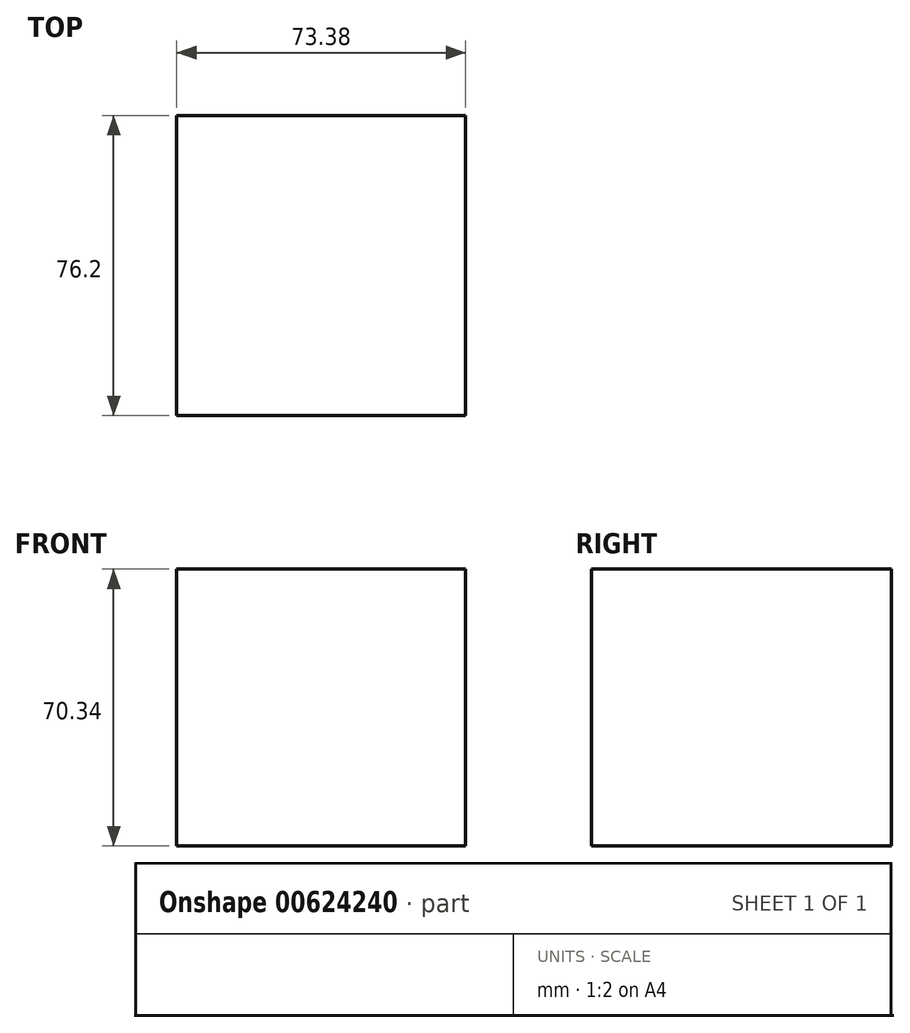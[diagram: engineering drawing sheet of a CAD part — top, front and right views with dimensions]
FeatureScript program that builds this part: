
annotation { "Feature Type Name" : "Feature", "Feature Type Description" : "" }
export const myFeature = defineFeature(function(context is Context, id is Id, definition is map)
    precondition{}
    {
        {
            var Q0;
            Q0=qCreatedBy(makeId("Front.planeOp"),FACE);
            var sketch = newSketch(context, id + "F0", { "sketchPlane" : qUnion([Q0])});
            skLineSegment(sketch, "E0.bottom", {"start": v(36.7, -35.17) * mm, "end": v(-36.7, -35.17) * mm});
            skLineSegment(sketch, "E0.top", {"start": v(36.7, 35.17) * mm, "end": v(-36.7, 35.17) * mm});
            skLineSegment(sketch, "E0.left", {"start": v(36.7, -35.17) * mm, "end": v(36.7, 35.17) * mm});
            skLineSegment(sketch, "E0.right", {"start": v(-36.7, -35.17) * mm, "end": v(-36.7, 35.17) * mm});
            skPoint(sketch, "E0.middle", {"position": v(0, 0) * mm});
            skSolve(sketch);
        }
        {
            var Q0;
            Q0 = qSketchRegion(id + "F0", true);
            extrude(context, id + "F1", {"entities" : qUnion([Q0]), "endBound" : BoundingType.SYMMETRIC, "depth" : 76.2 * mm, "offsetDistance" : 25.4 * mm});
        }
    });
